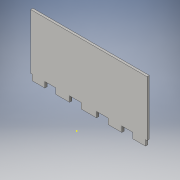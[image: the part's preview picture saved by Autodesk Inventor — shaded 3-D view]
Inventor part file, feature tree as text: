
AUTODESK INVENTOR PART (.ipt)
format: ipt  version: 2016 (Build 200138000, 138)  size: 124,416 bytes
history: native  units: in
note: dims shown in document units (in); Inventor stores cm internally (conversion verified against a paired STEP export)
features: sketch x3, extrude x2
ambient origin geometry x8: Origin, YZ Plane, XZ Plane, XY Plane, X Axis, Y Axis, Z Axis, Center Point
bodies: Solid1 (feature_tree)
feature tree (5):
  extrude  "Extrusion1"  Depth=0.09in TaperAngle=0.0deg
  extrude  "Extrusion2"  Depth=0.09in TaperAngle=0.0deg
  sketch  "Sketch3"
  sketch  "Sketch1"  dims[d0=2.2in d1=0.09in d2=0.0in]
  sketch  "Sketch2"  dims[d3=0.062in d5=0.09in d6=0.0in]
